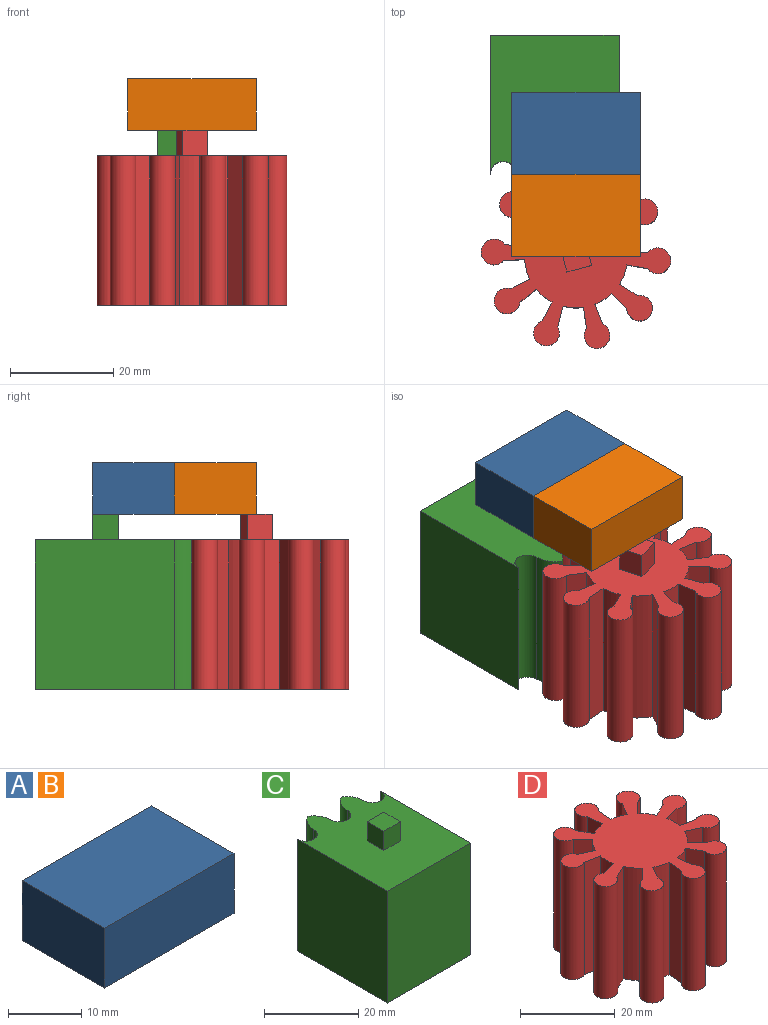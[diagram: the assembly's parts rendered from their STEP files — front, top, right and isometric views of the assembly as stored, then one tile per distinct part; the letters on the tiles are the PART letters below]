
ASSEMBLY  parts=4 mates=3
PART A: 6 faces, bbox 25x15.9x10 mm
  f0: plane 25x10mm, normal (0,1,0), area 250mm2, adj f1,f3,f4,f5
  f1: plane 15.92x10mm, normal (-1,0,0), area 159.1mm2, adj f0,f2,f4,f5
  f2: plane 25x10mm, normal (0,-1,0), area 250mm2, adj f1,f3,f4,f5
  f3: plane 15.92x10mm, normal (1,0,0), area 159.1mm2, adj f0,f2,f4,f5
  f4: plane 25x15.92mm, normal (0,0,1), area 397.9mm2, adj f0,f1,f2,f3
  f5: plane 25x15.92mm, normal (0,0,-1), area 397.9mm2, adj f0,f1,f2,f3
PART B: same geometry as A
PART C: 17 faces, bbox 25x31.3x34 mm
  f0: plane 31.33x25mm, normal (0,0,1), area 651.3mm2, adj f1,f2,f3,f4,f5,f6,f7,f8
  f1: cylinder r=2.5mm len=29mm, axis (0,0,-1), area 227.8mm2, adj f0,f2,f10,f11
  f2: plane 29x27mm, normal (-1,0,0), area 783mm2, adj f0,f1,f3,f11
  f3: plane 29x25mm, normal (0,-1,0), area 725mm2, adj f0,f2,f4,f11
  f4: plane 29x27mm, normal (1,0,0), area 783mm2, adj f0,f3,f5,f11
  f5: cylinder r=2.5mm len=29mm, axis (0,0,-1), area 227.8mm2, adj f0,f4,f6,f11
  f6: cylinder r=5mm len=29mm, axis (0,0,-1), area 151.8mm2, adj f0,f5,f7,f11
  f7: cylinder r=5mm len=29mm, axis (0,0,-1), area 151.8mm2, adj f0,f6,f8,f11
  f8: cylinder r=2.5mm len=29mm, axis (0,0,-1), area 227.8mm2, adj f0,f7,f9,f11
  f9: cylinder r=5mm len=29mm, axis (0,0,-1), area 151.8mm2, adj f0,f8,f10,f11
  f10: cylinder r=5mm len=29mm, axis (0,0,-1), area 151.8mm2, adj f0,f1,f9,f11
  f11: plane 31.33x25mm, normal (0,0,-1), area 676.3mm2, adj f1,f2,f3,f4,f5,f6,f7,f8
  f12: plane 5x5mm, normal (0,-1,0), area 25mm2, adj f0,f13,f15,f16
  f13: plane 5x5mm, normal (1,0,0), area 25mm2, adj f0,f12,f14,f16
  f14: plane 5x5mm, normal (0,1,0), area 25mm2, adj f0,f13,f15,f16
  f15: plane 5x5mm, normal (-1,0,0), area 25mm2, adj f0,f12,f14,f16
  f16: plane 5x5mm, normal (0,0,1), area 25mm2, adj f12,f13,f14,f15
PART D: 47 faces, bbox 35.3x36.8x34 mm
  f0: plane 29x4.01mm, normal (0.2,0.98,0), area 118.7mm2, adj f1,f39,f40,f41
  f1: cylinder r=10mm len=29mm, axis (0,0,-1), area 115.9mm2, adj f0,f2,f40,f41
  f2: plane 29x4.01mm, normal (0.2,-0.98,0), area 118.7mm2, adj f1,f3,f40,f41
  f3: cylinder r=2.5mm len=29mm, axis (0,0,-1), area 354.2mm2, adj f2,f4,f40,f41
  f4: plane 29x3.72mm, normal (-0.42,0.91,0), area 118.7mm2, adj f3,f5,f40,f41
  f5: cylinder r=10mm len=29mm, axis (0,0,-1), area 115.9mm2, adj f4,f6,f40,f41
  f6: plane 29x3.02mm, normal (0.74,-0.68,0), area 118.7mm2, adj f5,f7,f40,f41
  f7: cylinder r=2.5mm len=29mm, axis (0,0,-1), area 354.2mm2, adj f6,f8,f40,f41
  f8: plane 29x3.57mm, normal (-0.87,0.49,0), area 118.7mm2, adj f7,f9,f40,f41
  f9: cylinder r=10mm len=29mm, axis (0,0,-1), area 115.9mm2, adj f8,f10,f40,f41
  f10: plane 29x4.07mm, normal (0.99,-0.11,0), area 118.7mm2, adj f9,f11,f40,f41
  f11: cylinder r=2.5mm len=29mm, axis (0,0,-1), area 354.2mm2, adj f10,f12,f40,f41
  f12: plane 29x4.07mm, normal (-0.99,-0.11,0), area 118.7mm2, adj f11,f13,f40,f41
  f13: cylinder r=10mm len=29mm, axis (0,0,-1), area 115.9mm2, adj f12,f14,f40,f41
  f14: plane 29x3.57mm, normal (0.87,0.49,0), area 118.7mm2, adj f13,f15,f40,f41
  f15: cylinder r=2.5mm len=29mm, axis (0,0,-1), area 354.2mm2, adj f14,f16,f40,f41
  f16: plane 29x3.02mm, normal (-0.74,-0.68,0), area 118.7mm2, adj f15,f17,f40,f41
  f17: cylinder r=10mm len=29mm, axis (0,0,-1), area 115.9mm2, adj f16,f18,f40,f41
  f18: plane 29x3.72mm, normal (0.42,0.91,0), area 118.7mm2, adj f17,f19,f40,f41
  f19: cylinder r=2.5mm len=29mm, axis (0,0,-1), area 354.2mm2, adj f18,f20,f40,f41
  f20: plane 29x4.01mm, normal (-0.2,-0.98,0), area 118.7mm2, adj f19,f21,f40,f41
  f21: cylinder r=10mm len=29mm, axis (0,0,-1), area 115.9mm2, adj f20,f22,f40,f41
  f22: plane 29x4.01mm, normal (-0.2,0.98,0), area 118.7mm2, adj f21,f23,f40,f41
  f23: cylinder r=2.5mm len=29mm, axis (0,0,-1), area 354.2mm2, adj f22,f24,f40,f41
  f24: plane 29x3.72mm, normal (0.42,-0.91,0), area 118.7mm2, adj f23,f25,f40,f41
  f25: cylinder r=10mm len=29mm, axis (0,0,-1), area 115.9mm2, adj f24,f26,f40,f41
  f26: plane 29x3.02mm, normal (-0.74,0.68,0), area 118.7mm2, adj f25,f27,f40,f41
  f27: cylinder r=2.5mm len=29mm, axis (0,0,-1), area 354.2mm2, adj f26,f28,f40,f41
  f28: plane 29x3.57mm, normal (0.87,-0.49,0), area 118.7mm2, adj f27,f29,f40,f41
  f29: cylinder r=10mm len=29mm, axis (0,0,-1), area 115.9mm2, adj f28,f30,f40,f41
  f30: plane 29x4.07mm, normal (-0.99,0.11,0), area 118.7mm2, adj f29,f31,f40,f41
  f31: cylinder r=2.5mm len=29mm, axis (0,0,-1), area 354.2mm2, adj f30,f32,f40,f41
  f32: plane 29x4.07mm, normal (0.99,0.11,0), area 118.7mm2, adj f31,f33,f40,f41
  f33: cylinder r=10mm len=29mm, axis (0,0,-1), area 115.9mm2, adj f32,f34,f40,f41
  f34: plane 29x3.57mm, normal (-0.87,-0.49,0), area 118.7mm2, adj f33,f35,f40,f41
  f35: cylinder r=2.5mm len=29mm, axis (0,0,-1), area 354.2mm2, adj f34,f36,f40,f41
  f36: plane 29x3.02mm, normal (0.74,0.68,0), area 118.7mm2, adj f35,f37,f40,f41
  f37: cylinder r=10mm len=29mm, axis (0,0,-1), area 115.9mm2, adj f36,f38,f40,f41
  f38: plane 29x3.72mm, normal (-0.42,-0.91,0), area 118.7mm2, adj f37,f39,f40,f41
  f39: cylinder r=2.5mm len=29mm, axis (0,0,-1), area 354.2mm2, adj f0,f38,f40,f41
  f40: plane 36.83x35.27mm, normal (0,0,1), area 608.4mm2, adj f0,f1,f2,f3,f4,f5,f6,f7
  f41: plane 36.83x35.27mm, normal (0,0,-1), area 583.4mm2, adj f0,f1,f2,f3,f4,f5,f6,f7
  f42: plane 5x5mm, normal (0,-1,0), area 25mm2, adj f41,f43,f45,f46
  f43: plane 5x5mm, normal (-1,0,0), area 25mm2, adj f41,f42,f44,f46
  f44: plane 5x5mm, normal (0,1,0), area 25mm2, adj f41,f43,f45,f46
  f45: plane 5x5mm, normal (1,0,0), area 25mm2, adj f41,f42,f44,f46
  f46: plane 5x5mm, normal (0,0,-1), area 25mm2, adj f42,f43,f44,f45
PLACE A t=(104.58,-13.33,-125.27)mm
PLACE B t=(104.58,-29.25,-125.27)mm
PLACE C rot(axis=(0,0,1),180deg) t=(90.72,-31.93,-159.27)mm
PLACE D rot(axis=(0.99,0.13,0),180deg) t=(104.58,-37.21,-130.27)mm
MATE slider C.f2 <-> A.f3  axis (1,0,0) through (112.95,-21.29,-125.27)mm
MATE revolute D.f21 <-> B.f5  axis (0,0,1) through (104.58,-37.21,-125.27)mm
MATE fastened A.f4 <-> B.f4  axis (0,0,1) through (104.58,-21.29,-115.27)mm
